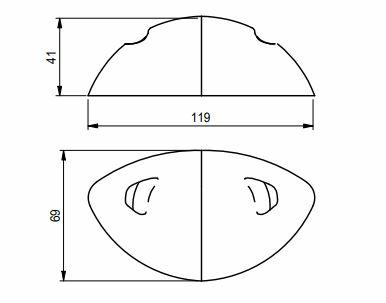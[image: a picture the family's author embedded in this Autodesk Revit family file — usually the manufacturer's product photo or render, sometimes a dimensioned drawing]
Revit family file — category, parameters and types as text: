
# Revit family: R-MBD-479
name_source: partatom
category: Portes
units: mm (PartAtom-declared; Revit-internal decimal feet)

## family parameters
Couper avec des vides une fois chargée = Non
Hôte = Mur
Partagée = Non
Repère de localisation dans la pièce = Oui
Toujours verticalement = Oui

## types (1)
- MBD-479
    1 Vantail = Non
    2 Vantaux = Oui
    A.E.V = non
    Acoustique = non
    Anti-Effraction = non
    Certification = D.A.S. Mode 2 certifié NF
    Code_MAJ = 2303130305MBD479
    Coloris_Chants = BER
    Coloris_Dormant = Hêtre
    Coloris_Face_Cote_Oppose_Ouverture = Prépeint
    Coloris_Face_Cote_Ouverture = Prépeint
    Construction analytique = <Aucun>
    DAS = Oui
    DC Larg Feuillure = 12 mm  [stored 0.0393701 ft]
    DC Pivot Vantail = 60 mm  [stored 0.19685 ft]
    Description = Bloc-porte bois D.A.S. 2 vantaux avec pivots linteaux motorisés encastrés, double action / va-et-vient, EI30, D.A.S. certifié NF, sur huisserie bois
    Définir les propriétés thermiques par = Type schématique
    Ep Profil Pose Tunnel = 118 mm
    Ep Strat Vantail = 1 mm  [stored 0.00328084 ft]
    Ep Vantail = 51 mm  [stored 0.167323 ft]
    Epaisseur_Rainure à brique = 8 mm  [stored 0.0262467 ft]
    Fabricant = MALERBA
    Fiche_Produit = MBD-479
    Fileur = Non
    Hauteur_Tableau = 2125 mm
    Hauteur_Vantaux_Souhaitée = 2040 mm  [stored 6.69291 ft]
    Jeu_1 = 0 mm  [stored 0 ft]
    Jeu_2 = 0 mm  [stored 0 ft]
    Jeu_Côté_Articulation_Vantail = 8 mm  [stored 0.0262467 ft]
    Jeu_Côté_Fermeture_Vantail = 8 mm  [stored 0.0262467 ft]
    Jeu_Haut = 3 mm  [stored 0.00984252 ft]
    Larg Profil = 58 mm  [stored 0.190289 ft]
    Larg Profil Avec Fileur = 20 mm  [stored 0.0656168 ft]
    Larg Profil Trav = 76 mm  [stored 0.249344 ft]
    Largeur = 0 mm  [stored 0 ft]
    Largeur_Vantail_Semi_Fixe_Souhaitée = 930 mm  [stored 3.05118 ft]
    Largeur_Vantail_Service_Souhaitée = 930 mm  [stored 3.05118 ft]
    Mat APD = Caoutchouc noir
    Mat Parclose = BER 2
    Mat Parclose Métal = Peinture Laquée PMT - Blanc Pur - RAL 9010
    Materiaux_Dominant = Bois
    Modèle = Va et vient
    Montant_VV = Oui
    Note d'identification = 2V EI30 DAS - LINTEAU MOTORISE - HUISSERIE BOIS
    Pivot linteau motorisé = Oui
    Profondeur_Rainure à brique = 5 mm  [stored 0.0164042 ft]
    Reference_Commerciale = 1V SP51/DA LINTEAU OP
    Resistance_Feu = EI30
    Sans_Montants = Non
    Sens_Feu = Recto / Verso
    Thermique (W/m2.°K) = 0
    URL = https://www.malerba.fr
    X_Axe Pivot = 114 mm  [stored 0.374016 ft]
    X_DC seuil = 9 mm  [stored 0.0295276 ft]
    X_Inv_DC Larg Feuillure_1V Montant = 0 mm  [stored 0 ft]

note: [stored X ft] marks values corroborated as IEEE doubles in the binary element streams (Revit-internal decimal feet)

## geometry (parser evidence)
native form markers: Blend x14
no freeform markers — native parametric forms only
